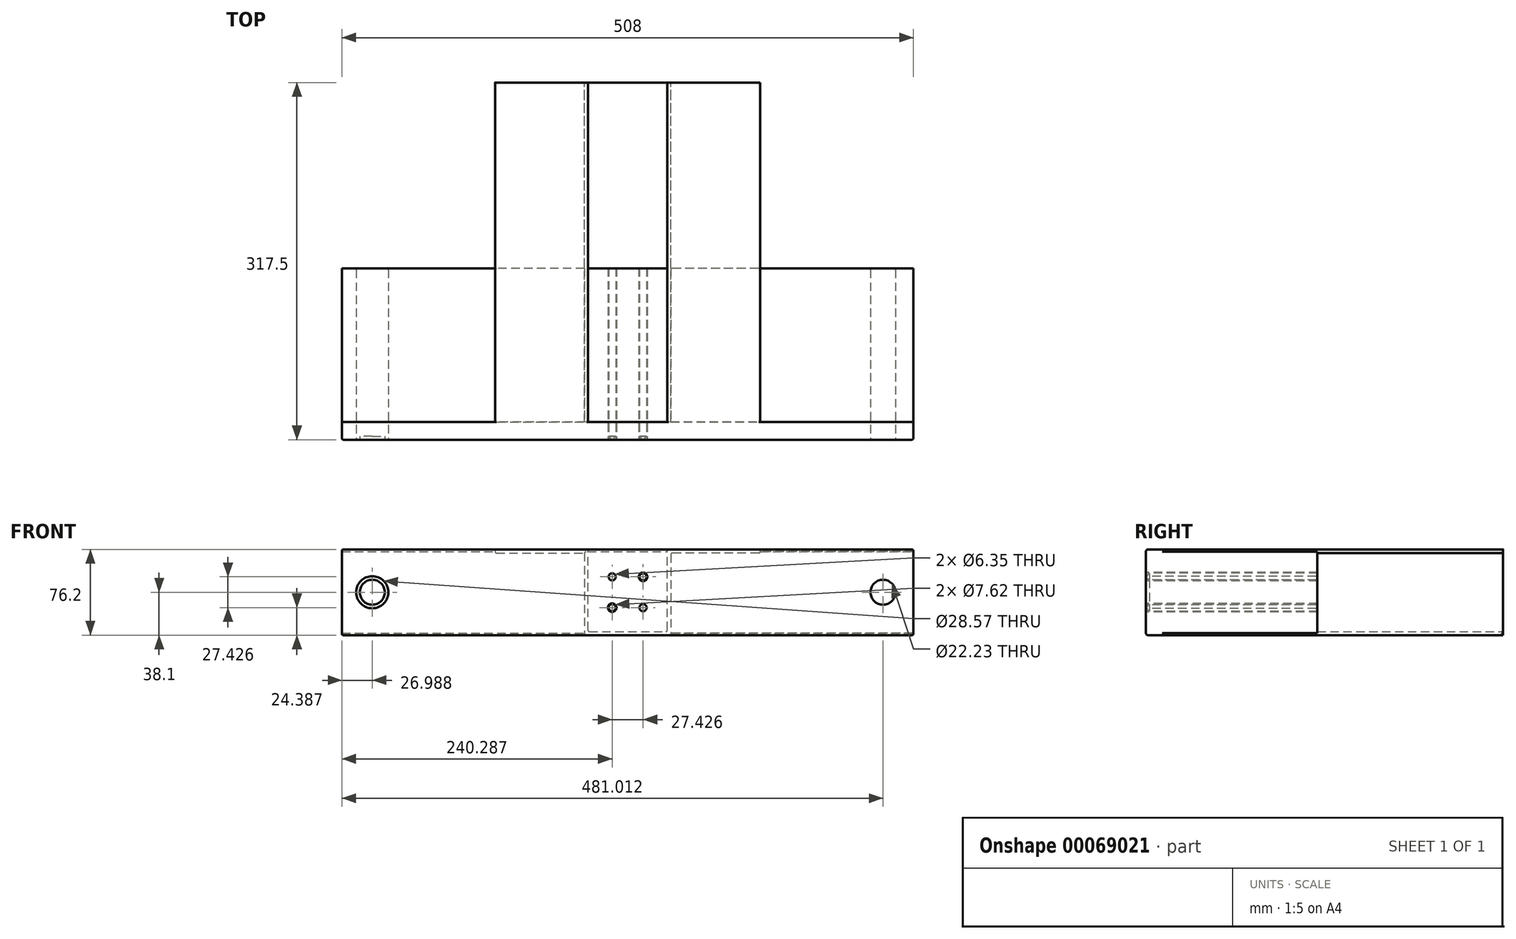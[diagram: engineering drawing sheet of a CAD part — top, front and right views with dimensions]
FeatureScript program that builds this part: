
annotation { "Feature Type Name" : "Feature", "Feature Type Description" : "" }
export const myFeature = defineFeature(function(context is Context, id is Id, definition is map)
    precondition{}
    {
        {
            var Q0;
            Q0=qCreatedBy(makeId("Front.planeOp"),FACE);
            var sketch = newSketch(context, id + "F0", { "sketchPlane" : qUnion([Q0])});
            skLineSegment(sketch, "E0.bottom", {"start": v(-508, 76.2) * mm, "end": v(0, 76.2) * mm});
            skLineSegment(sketch, "E0.top", {"start": v(-508, 0) * mm, "end": v(0, 0) * mm});
            skLineSegment(sketch, "E0.left", {"start": v(-508, 76.2) * mm, "end": v(-508, 0) * mm});
            skLineSegment(sketch, "E0.right", {"start": v(0, 76.2) * mm, "end": v(0, 0) * mm});
            skSolve(sketch);
        }
        {
            var Q0;
            Q0=makeQuery(id+"F0.imprint","IMPRINT",FACE,{"disambiguationData":[TD([[makeQuery(id+"F0.imprint","IMPRINT",EDGE,{"derivedFrom":sQuery(id+"F0.wireOp",EDGE,"E0.bottom")}),-1.0]])]});
            extrude(context, id + "F1", {"entities" : qUnion([Q0]), "depth" : 317.5 * mm});
        }
        {
            var Q0;
            Q0=makeQuery(id+"F1.opExtrude","SWEPT_FACE",FACE,{"disambiguationData":[OSD([sQuery(id+"F0.wireOp",EDGE,"E0.left")])]});
            var sketch = newSketch(context, id + "F2", { "sketchPlane" : qUnion([Q0])});
            skCircle(sketch, "E1", {"center": v(315.64, 74.34) * mm, "radius": 1.86 * mm});
            skCircle(sketch, "E2", {"center": v(312.47, 71.17) * mm, "radius": 1.86 * mm});
            skLineSegment(sketch, "E3.0", {"start": v(317.5, 76.2) * mm, "end": v(317.5, 0) * mm});
            skLineSegment(sketch, "E3.1", {"start": v(317.5, 76.2) * mm, "end": v(0, 76.2) * mm});
            skLineSegment(sketch, "E3.2", {"start": v(317.5, 0) * mm, "end": v(0, 0) * mm});
            skLineSegment(sketch, "E4", {"start": v(301.63, 76.2) * mm, "end": v(301.63, 73.03) * mm});
            skLineSegment(sketch, "E5", {"start": v(301.63, 73.03) * mm, "end": v(314.33, 73.03) * mm});
            skLineSegment(sketch, "E6", {"start": v(314.33, 73.03) * mm, "end": v(314.33, 3.18) * mm});
            skLineSegment(sketch, "E7", {"start": v(314.33, 3.18) * mm, "end": v(301.63, 3.18) * mm});
            skLineSegment(sketch, "E8", {"start": v(301.63, 3.18) * mm, "end": v(301.63, 0) * mm});
            skLineSegment(sketch, "E9", {"start": v(317.5, 38.1) * mm, "end": v(282.6, 38.1) * mm, "construction": true});
            skPoint(sketch, "E9.endSnap0", {"position": v(317.5, 38.1) * mm});
            skCircle(sketch, "E10.MirrorC", {"center": v(312.47, 5.03) * mm, "radius": 1.86 * mm});
            skCircle(sketch, "E11.MirrorC", {"center": v(315.64, 1.86) * mm, "radius": 1.86 * mm});
            skSolve(sketch);
        }
        {
            var Q0;
            Q0=makeQuery(id+"F1.opExtrude","CAP_FACE",FACE,{"disambiguationData":[OSD([sQuery(id+"F0.wireOp",EDGE,"E0.bottom"),sQuery(id+"F0.wireOp",EDGE,"E0.top"),sQuery(id+"F0.wireOp",EDGE,"E0.left"),sQuery(id+"F0.wireOp",EDGE,"E0.right")])],"isStart":true});
            var sketch = newSketch(context, id + "F3", { "sketchPlane" : qUnion([Q0])});
            skLineSegment(sketch, "E12.0", {"start": v(508, 76.2) * mm, "end": v(0, 76.2) * mm});
            skLineSegment(sketch, "E12.1", {"start": v(0, 76.2) * mm, "end": v(0, 0) * mm});
            skLineSegment(sketch, "E12.2", {"start": v(508, 0) * mm, "end": v(0, 0) * mm});
            skLineSegment(sketch, "E12.3", {"start": v(508, 76.2) * mm, "end": v(508, 0) * mm});
            skLineSegment(sketch, "E13", {"start": v(136.13, 76.2) * mm, "end": v(136.13, 73.03) * mm});
            skLineSegment(sketch, "E14", {"start": v(136.13, 73.03) * mm, "end": v(215.5, 73.03) * mm});
            skLineSegment(sketch, "E15", {"start": v(215.5, 73.03) * mm, "end": v(215.5, 0) * mm});
            skLineSegment(sketch, "E16", {"start": v(215.5, 0) * mm, "end": v(254, 0) * mm});
            skLineSegment(sketch, "E17", {"start": v(254, 0) * mm, "end": v(254, 3.17) * mm});
            skLineSegment(sketch, "E18", {"start": v(254, 3.17) * mm, "end": v(218.68, 3.17) * mm});
            skLineSegment(sketch, "E19", {"start": v(218.68, 3.17) * mm, "end": v(218.68, 76.2) * mm});
            skLineSegment(sketch, "E20", {"start": v(218.68, 76.2) * mm, "end": v(136.13, 76.2) * mm});
            skLineSegment(sketch, "E21", {"start": v(254, 76.2) * mm, "end": v(254, 0) * mm, "construction": true});
            skLineSegment(sketch, "E22.MirrorCS", {"start": v(292.5, 0) * mm, "end": v(254, 0) * mm});
            skLineSegment(sketch, "E23.MirrorCS", {"start": v(254, 3.17) * mm, "end": v(289.32, 3.17) * mm});
            skLineSegment(sketch, "E24.MirrorCS", {"start": v(289.32, 3.17) * mm, "end": v(289.32, 76.2) * mm});
            skLineSegment(sketch, "E25.MirrorCS", {"start": v(292.5, 73.03) * mm, "end": v(292.5, 0) * mm});
            skLineSegment(sketch, "E26.MirrorCS", {"start": v(289.32, 76.2) * mm, "end": v(371.87, 76.2) * mm});
            skLineSegment(sketch, "E27.MirrorCS", {"start": v(371.87, 73.03) * mm, "end": v(292.5, 73.03) * mm});
            skLineSegment(sketch, "E28.MirrorCS", {"start": v(371.87, 76.2) * mm, "end": v(371.87, 73.03) * mm});
            skSolve(sketch);
        }
        {
            var Q0;
            {var subQ2=sQuery(id+"F2.wireOp",EDGE,"E4");Q0=makeQuery(id+"F2.imprint","IMPRINT",FACE,{"disambiguationData":[TD([[makeQuery(id+"F2.imprint","IMPRINT",EDGE,{"derivedFrom":subQ2}),-1.0]])]});}
            var Q1;
            {var subQ0=sQuery(id+"F2.wireOp",EDGE,"E3.1");var subQ1=sQuery(id+"F2.wireOp",EDGE,"E1");var subQ2=makeQuery(id+"F2.imprint","INTERSECT",VERTEX,{"derivedFrom":[subQ1,subQ0]});Q1=makeQuery(id+"F2.imprint","IMPRINT",FACE,{"disambiguationData":[TD([[makeQuery(id+"F2.imprint","IMPRINT",EDGE,{"disambiguationData":[TD([[subQ2,1.0]])],"derivedFrom":subQ1}),-1.0]])]});}
            var Q2;
            {var subQ0=sQuery(id+"F2.wireOp",EDGE,"E2");var subQ1=makeQuery(id+"F2.imprint","INTERSECT",VERTEX,{"derivedFrom":[subQ0,sQuery(id+"F2.wireOp",EDGE,"E5")]});Q2=makeQuery(id+"F2.imprint","IMPRINT",FACE,{"disambiguationData":[TD([[makeQuery(id+"F2.imprint","IMPRINT",EDGE,{"disambiguationData":[TD([[subQ1,1.0]])],"derivedFrom":subQ0}),1.0]])]});}
            var Q3;
            {var subQ0=sQuery(id+"F2.wireOp",EDGE,"E3.2");var subQ1=sQuery(id+"F2.wireOp",EDGE,"E3.0");var subQ2=makeQuery(id+"F2.imprint","INTERSECT",VERTEX,{"derivedFrom":[subQ1,subQ0]});Q3=makeQuery(id+"F2.imprint","IMPRINT",FACE,{"disambiguationData":[TD([[makeQuery(id+"F2.imprint","IMPRINT",EDGE,{"disambiguationData":[TD([[subQ2,1.0]])],"derivedFrom":subQ1}),-1.0]])]});}
            var Q4;
            {var subQ0=sQuery(id+"F2.wireOp",EDGE,"E10.MirrorC");var subQ1=makeQuery(id+"F2.imprint","INTERSECT",VERTEX,{"derivedFrom":[sQuery(id+"F2.wireOp",EDGE,"E6"),subQ0]});Q4=makeQuery(id+"F2.imprint","IMPRINT",FACE,{"disambiguationData":[TD([[makeQuery(id+"F2.imprint","IMPRINT",EDGE,{"disambiguationData":[TD([[subQ1,-1.0]])],"derivedFrom":subQ0}),-1.0]])]});}
            extrude(context, id + "F4", {"entities" : qUnion([Q0, Q1, Q2, Q3, Q4]), "operationType" : NewBodyOperationType.REMOVE, "endBound" : BoundingType.THROUGH_ALL, "oppositeDirection" : true, "depth" : 25.4 * mm});
        }
        {
            var Q0;
            Q0=makeQuery(id+"F3.imprint","IMPRINT",FACE,{"disambiguationData":[TD([[makeQuery(id+"F3.imprint","IMPRINT",EDGE,{"derivedFrom":sQuery(id+"F3.wireOp",EDGE,"E13")}),1.0]])]});
            var Q1;
            Q1=makeQuery(id+"F3.imprint","IMPRINT",FACE,{"disambiguationData":[TD([[makeQuery(id+"F3.imprint","IMPRINT",EDGE,{"derivedFrom":sQuery(id+"F3.wireOp",EDGE,"E17")}),-1.0]])]});
            var Q2;
            Q2=makeQuery(id+"F4.boolean.opBoolean","COPY",FACE,{"derivedFrom":makeQuery(id+"F4.opExtrude","SWEPT_FACE",FACE,{"disambiguationData":[OSD([sQuery(id+"F2.wireOp",EDGE,"E6")])]})});
            extrude(context, id + "F5", {"entities" : qUnion([Q0, Q1]), "operationType" : NewBodyOperationType.ADD, "endBound" : BoundingType.UP_TO_SURFACE, "oppositeDirection" : true, "endBoundEntityFace" : qUnion([Q2]), "depth" : 25.4 * mm});
        }
        {
            var Q0;
            Q0=makeQuery(id+"F1.opExtrude","CAP_FACE",FACE,{"disambiguationData":[OSD([sQuery(id+"F0.wireOp",EDGE,"E0.bottom"),sQuery(id+"F0.wireOp",EDGE,"E0.top"),sQuery(id+"F0.wireOp",EDGE,"E0.left"),sQuery(id+"F0.wireOp",EDGE,"E0.right")])],"isStart":false});
            var sketch = newSketch(context, id + "F6", { "sketchPlane" : qUnion([Q0])});
            skLineSegment(sketch, "E29.0", {"start": v(0, 0) * mm, "end": v(-508, 0) * mm});
            skLineSegment(sketch, "E29.1", {"start": v(0, 74.34) * mm, "end": v(-508, 74.34) * mm});
            skLineSegment(sketch, "E30", {"start": v(0, 1.86) * mm, "end": v(-508, 74.34) * mm, "construction": true});
            skCircle(sketch, "E31", {"center": v(-254, 38.1) * mm, "radius": 19.4 * mm, "construction": true});
            skCircle(sketch, "E32", {"center": v(-240.29, 24.39) * mm, "radius": 3.81 * mm});
            skCircle(sketch, "E33", {"center": v(-240.29, 24.39) * mm, "radius": 3.18 * mm});
            skLineSegment(sketch, "E34", {"start": v(-254, 1.86) * mm, "end": v(-254, 74.34) * mm, "construction": true});
            skLineSegment(sketch, "E35", {"start": v(-303.81, 38.1) * mm, "end": v(-196.21, 38.1) * mm, "construction": true});
            skLineSegment(sketch, "E36", {"start": v(-254, 38.1) * mm, "end": v(-240.29, 24.39) * mm, "construction": true});
            skCircle(sketch, "E37.MirrorC", {"center": v(-267.71, 24.39) * mm, "radius": 3.81 * mm});
            skCircle(sketch, "E38.MirrorC", {"center": v(-267.71, 24.39) * mm, "radius": 3.18 * mm});
            skCircle(sketch, "E39.MirrorC", {"center": v(-267.71, 51.81) * mm, "radius": 3.81 * mm});
            skCircle(sketch, "E40.MirrorC", {"center": v(-267.71, 51.81) * mm, "radius": 3.18 * mm});
            skCircle(sketch, "E41.MirrorC", {"center": v(-240.29, 51.81) * mm, "radius": 3.81 * mm});
            skCircle(sketch, "E42.MirrorC", {"center": v(-240.29, 51.81) * mm, "radius": 3.18 * mm});
            skSolve(sketch);
        }
        {
            var Q0;
            Q0=makeQuery(id+"F6.imprint","IMPRINT",FACE,{"disambiguationData":[TD([[makeQuery(id+"F6.imprint","IMPRINT",EDGE,{"derivedFrom":sQuery(id+"F6.wireOp",EDGE,"E33")}),1.0]])]});
            var Q1;
            Q1=makeQuery(id+"F6.imprint","IMPRINT",FACE,{"disambiguationData":[TD([[makeQuery(id+"F6.imprint","IMPRINT",EDGE,{"derivedFrom":sQuery(id+"F6.wireOp",EDGE,"E38.MirrorC")}),-1.0]])]});
            var Q2;
            Q2=makeQuery(id+"F6.imprint","IMPRINT",FACE,{"disambiguationData":[TD([[makeQuery(id+"F6.imprint","IMPRINT",EDGE,{"derivedFrom":sQuery(id+"F6.wireOp",EDGE,"E40.MirrorC")}),1.0]])]});
            var Q3;
            Q3=makeQuery(id+"F6.imprint","IMPRINT",FACE,{"disambiguationData":[TD([[makeQuery(id+"F6.imprint","IMPRINT",EDGE,{"derivedFrom":sQuery(id+"F6.wireOp",EDGE,"E42.MirrorC")}),-1.0]])]});
            extrude(context, id + "F7", {"entities" : qUnion([Q0, Q1, Q2, Q3]), "operationType" : NewBodyOperationType.REMOVE, "endBound" : BoundingType.THROUGH_ALL, "oppositeDirection" : true, "depth" : 25.4 * mm});
        }
        {
            var Q0;
            Q0=makeQuery(id+"F7.boolean.opBoolean","COPY",EDGE,{"derivedFrom":makeQuery(id+"F7.opExtrude","CAP_EDGE",EDGE,{"disambiguationData":[OSD([sQuery(id+"F6.wireOp",EDGE,"E33")])],"isStart":true})});
            var Q1;
            Q1=makeQuery(id+"F7.boolean.opBoolean","COPY",EDGE,{"derivedFrom":makeQuery(id+"F7.opExtrude","CAP_EDGE",EDGE,{"disambiguationData":[OSD([sQuery(id+"F6.wireOp",EDGE,"E38.MirrorC")])],"isStart":true})});
            var Q2;
            Q2=makeQuery(id+"F7.boolean.opBoolean","COPY",EDGE,{"derivedFrom":makeQuery(id+"F7.opExtrude","CAP_EDGE",EDGE,{"disambiguationData":[OSD([sQuery(id+"F6.wireOp",EDGE,"E40.MirrorC")])],"isStart":true})});
            var Q3;
            Q3=makeQuery(id+"F7.boolean.opBoolean","COPY",EDGE,{"derivedFrom":makeQuery(id+"F7.opExtrude","CAP_EDGE",EDGE,{"disambiguationData":[OSD([sQuery(id+"F6.wireOp",EDGE,"E42.MirrorC")])],"isStart":true})});
            chamfer(context, id + "F8", {"entities" : qUnion([Q0, Q1, Q2, Q3]), "width" : 3.17 * mm, "tangentPropagation" : true});
        }
        {
            var Q0;
            Q0=makeQuery(id+"F1.opExtrude","CAP_FACE",FACE,{"disambiguationData":[OSD([sQuery(id+"F0.wireOp",EDGE,"E0.bottom"),sQuery(id+"F0.wireOp",EDGE,"E0.top"),sQuery(id+"F0.wireOp",EDGE,"E0.left"),sQuery(id+"F0.wireOp",EDGE,"E0.right")])],"isStart":false});
            var sketch = newSketch(context, id + "F9", { "sketchPlane" : qUnion([Q0])});
            skLineSegment(sketch, "E43.0", {"start": v(0, 1.86) * mm, "end": v(-508, 1.86) * mm});
            skLineSegment(sketch, "E43.1", {"start": v(0, 74.34) * mm, "end": v(-508, 74.34) * mm});
            skLineSegment(sketch, "E44", {"start": v(-254, 1.86) * mm, "end": v(-254, 74.34) * mm, "construction": true});
            skLineSegment(sketch, "E45.0", {"start": v(0, 74.34) * mm, "end": v(0, 1.86) * mm});
            skLineSegment(sketch, "E45.1", {"start": v(-508, 74.34) * mm, "end": v(-508, 1.86) * mm});
            skLineSegment(sketch, "E46", {"start": v(0, 38.1) * mm, "end": v(-254, 38.1) * mm, "construction": true});
            skCircle(sketch, "E47", {"center": v(-26.99, 38.1) * mm, "radius": 11.11 * mm});
            skCircle(sketch, "E48.MirrorC", {"center": v(-481.01, 38.1) * mm, "radius": 11.11 * mm});
            skCircle(sketch, "E49", {"center": v(-26.99, 38.1) * mm, "radius": 14.29 * mm});
            skCircle(sketch, "E50.MirrorC", {"center": v(-481.01, 38.1) * mm, "radius": 14.29 * mm});
            skSolve(sketch);
        }
        {
            var Q0;
            Q0=makeQuery(id+"F9.imprint","IMPRINT",FACE,{"disambiguationData":[TD([[makeQuery(id+"F9.imprint","IMPRINT",EDGE,{"derivedFrom":sQuery(id+"F9.wireOp",EDGE,"E47")}),-1.0]])]});
            var Q1;
            Q1=makeQuery(id+"F9.imprint","IMPRINT",FACE,{"disambiguationData":[TD([[makeQuery(id+"F9.imprint","IMPRINT",EDGE,{"derivedFrom":sQuery(id+"F9.wireOp",EDGE,"E50.MirrorC")}),-1.0]])]});
            extrude(context, id + "F10", {"entities" : qUnion([Q0, Q1]), "operationType" : NewBodyOperationType.ADD, "oppositeDirection" : true, "depth" : 152.4 * mm});
        }
        {
            var Q0;
            Q0=makeQuery(id+"F9.imprint","IMPRINT",FACE,{"disambiguationData":[TD([[makeQuery(id+"F9.imprint","IMPRINT",EDGE,{"derivedFrom":sQuery(id+"F9.wireOp",EDGE,"E47")}),1.0]])]});
            var Q1;
            Q1=makeQuery(id+"F9.imprint","IMPRINT",FACE,{"disambiguationData":[TD([[makeQuery(id+"F9.imprint","IMPRINT",EDGE,{"derivedFrom":sQuery(id+"F9.wireOp",EDGE,"E48.MirrorC")}),-1.0]])]});
            extrude(context, id + "F11", {"entities" : qUnion([Q0, Q1]), "operationType" : NewBodyOperationType.REMOVE, "endBound" : BoundingType.THROUGH_ALL, "oppositeDirection" : true, "depth" : 25.4 * mm});
        }
        {
            var Q0;
            Q0=makeQuery(id+"F4.boolean.opBoolean","COPY",EDGE,{"derivedFrom":makeQuery(id+"F4.opExtrude","CAP_EDGE",EDGE,{"disambiguationData":[OSD([sQuery(id+"F2.wireOp",EDGE,"E8")])],"isStart":true})});
            var Q1;
            Q1=makeQuery(id+"F4.boolean.opBoolean","COPY",EDGE,{"derivedFrom":makeQuery(id+"F4.opExtrude","CAP_EDGE",EDGE,{"disambiguationData":[OSD([sQuery(id+"F2.wireOp",EDGE,"E4")])],"isStart":true})});
            var Q2;
            Q2=makeQuery(id+"F4.boolean.opBoolean","INTERSECT",EDGE,{"derivedFrom":[makeQuery(id+"F1.opExtrude","SWEPT_FACE",FACE,{"disambiguationData":[OSD([sQuery(id+"F0.wireOp",EDGE,"E0.right")])]}),makeQuery(id+"F4.opExtrude","SWEPT_FACE",FACE,{"disambiguationData":[OSD([sQuery(id+"F2.wireOp",EDGE,"E8")])]})]});
            var Q3;
            Q3=makeQuery(id+"F4.boolean.opBoolean","INTERSECT",EDGE,{"derivedFrom":[makeQuery(id+"F1.opExtrude","SWEPT_FACE",FACE,{"disambiguationData":[OSD([sQuery(id+"F0.wireOp",EDGE,"E0.right")])]}),makeQuery(id+"F4.opExtrude","SWEPT_FACE",FACE,{"disambiguationData":[OSD([sQuery(id+"F2.wireOp",EDGE,"E4")])]})]});
            var Q4;
            Q4=makeQuery(id+"F10.opExtrude","CAP_EDGE",EDGE,{"disambiguationData":[OSD([sQuery(id+"F9.wireOp",EDGE,"E47")])],"isStart":false});
            var Q5;
            Q5=makeQuery(id+"F11.boolean.opBoolean","COPY",EDGE,{"derivedFrom":makeQuery(id+"F11.opExtrude","CAP_EDGE",EDGE,{"disambiguationData":[OSD([sQuery(id+"F9.wireOp",EDGE,"E47")])],"isStart":true})});
            var Q6;
            Q6=makeQuery(id+"F11.boolean.opBoolean","COPY",EDGE,{"derivedFrom":makeQuery(id+"F11.opExtrude","CAP_EDGE",EDGE,{"disambiguationData":[OSD([sQuery(id+"F9.wireOp",EDGE,"E48.MirrorC")])],"isStart":true})});
            var Q7;
            Q7=makeQuery(id+"F10.opExtrude","CAP_EDGE",EDGE,{"disambiguationData":[OSD([sQuery(id+"F9.wireOp",EDGE,"E48.MirrorC")])],"isStart":false});
            var Q8;
            Q8=makeQuery(id+"F10.opExtrude","CAP_EDGE",EDGE,{"disambiguationData":[OSD([sQuery(id+"F9.wireOp",EDGE,"E50.MirrorC")])],"isStart":false});
            var Q9;
            Q9=makeQuery(id+"F10.opExtrude","CAP_EDGE",EDGE,{"disambiguationData":[OSD([sQuery(id+"F9.wireOp",EDGE,"E49")])],"isStart":false});
            var Q10;
            {var subQ0=sQuery(id+"F2.wireOp",EDGE,"E8");Q10=makeQuery(id+"F5.boolean.opBoolean","SPLIT",EDGE,{"disambiguationData":[TD([makeQuery(id+"F1.opExtrude","SWEPT_FACE",FACE,{"disambiguationData":[OSD([sQuery(id+"F0.wireOp",EDGE,"E0.right")])]})])],"derivedFrom":makeQuery(id+"F4.boolean.opBoolean","COPY",EDGE,{"derivedFrom":makeQuery(id+"F4.opExtrude","SWEPT_EDGE",EDGE,{"disambiguationData":[OSD([sQuery(id+"F2.wireOp",EDGE,"E3.2"),subQ0])]})})});}
            var Q11;
            {var subQ0=sQuery(id+"F2.wireOp",EDGE,"E8");var subQ1=sQuery(id+"F2.wireOp",EDGE,"E7");Q11=makeQuery(id+"F5.boolean.opBoolean","SPLIT",EDGE,{"disambiguationData":[TD([makeQuery(id+"F1.opExtrude","SWEPT_FACE",FACE,{"disambiguationData":[OSD([sQuery(id+"F0.wireOp",EDGE,"E0.right")])]})])],"derivedFrom":makeQuery(id+"F4.boolean.opBoolean","COPY",EDGE,{"derivedFrom":makeQuery(id+"F4.opExtrude","SWEPT_EDGE",EDGE,{"disambiguationData":[OSD([subQ1,subQ0])]})})});}
            var Q12;
            {var subQ0=sQuery(id+"F2.wireOp",EDGE,"E5");var subQ1=sQuery(id+"F2.wireOp",EDGE,"E4");Q12=makeQuery(id+"F5.boolean.opBoolean","SPLIT",EDGE,{"disambiguationData":[TD([makeQuery(id+"F1.opExtrude","SWEPT_FACE",FACE,{"disambiguationData":[OSD([sQuery(id+"F0.wireOp",EDGE,"E0.right")])]})])],"derivedFrom":makeQuery(id+"F4.boolean.opBoolean","COPY",EDGE,{"derivedFrom":makeQuery(id+"F4.opExtrude","SWEPT_EDGE",EDGE,{"disambiguationData":[OSD([subQ1,subQ0])]})})});}
            var Q13;
            {var subQ0=sQuery(id+"F2.wireOp",EDGE,"E4");Q13=makeQuery(id+"F5.boolean.opBoolean","SPLIT",EDGE,{"disambiguationData":[TD([makeQuery(id+"F1.opExtrude","SWEPT_FACE",FACE,{"disambiguationData":[OSD([sQuery(id+"F0.wireOp",EDGE,"E0.right")])]})])],"derivedFrom":makeQuery(id+"F4.boolean.opBoolean","COPY",EDGE,{"derivedFrom":makeQuery(id+"F4.opExtrude","SWEPT_EDGE",EDGE,{"disambiguationData":[OSD([sQuery(id+"F2.wireOp",EDGE,"E3.1"),subQ0])]})})});}
            var Q14;
            {var subQ0=sQuery(id+"F2.wireOp",EDGE,"E5");var subQ1=sQuery(id+"F2.wireOp",EDGE,"E4");Q14=makeQuery(id+"F5.boolean.opBoolean","SPLIT",EDGE,{"disambiguationData":[TD([makeQuery(id+"F1.opExtrude","SWEPT_FACE",FACE,{"disambiguationData":[OSD([sQuery(id+"F0.wireOp",EDGE,"E0.left")])]})])],"derivedFrom":makeQuery(id+"F4.boolean.opBoolean","COPY",EDGE,{"derivedFrom":makeQuery(id+"F4.opExtrude","SWEPT_EDGE",EDGE,{"disambiguationData":[OSD([subQ1,subQ0])]})})});}
            var Q15;
            {var subQ0=sQuery(id+"F2.wireOp",EDGE,"E4");Q15=makeQuery(id+"F5.boolean.opBoolean","SPLIT",EDGE,{"disambiguationData":[TD([makeQuery(id+"F1.opExtrude","SWEPT_FACE",FACE,{"disambiguationData":[OSD([sQuery(id+"F0.wireOp",EDGE,"E0.left")])]})])],"derivedFrom":makeQuery(id+"F4.boolean.opBoolean","COPY",EDGE,{"derivedFrom":makeQuery(id+"F4.opExtrude","SWEPT_EDGE",EDGE,{"disambiguationData":[OSD([sQuery(id+"F2.wireOp",EDGE,"E3.1"),subQ0])]})})});}
            var Q16;
            Q16=makeQuery(id+"F5.opExtrude","SWEPT_EDGE",EDGE,{"disambiguationData":[OSD([sQuery(id+"F3.wireOp",EDGE,"E27.MirrorCS"),sQuery(id+"F3.wireOp",EDGE,"E28.MirrorCS")])]});
            var Q17;
            Q17=makeQuery(id+"F5.opExtrude","SWEPT_EDGE",EDGE,{"disambiguationData":[OSD([sQuery(id+"F3.wireOp",EDGE,"E12.0"),sQuery(id+"F3.wireOp",EDGE,"E26.MirrorCS"),sQuery(id+"F3.wireOp",EDGE,"E28.MirrorCS")])]});
            var Q18;
            Q18=makeQuery(id+"F5.opExtrude","CAP_EDGE",EDGE,{"disambiguationData":[OSD([sQuery(id+"F3.wireOp",EDGE,"E27.MirrorCS")])],"isStart":true});
            var Q19;
            Q19=makeQuery(id+"F5.opExtrude","CAP_EDGE",EDGE,{"disambiguationData":[OSD([sQuery(id+"F3.wireOp",EDGE,"E26.MirrorCS")])],"isStart":true});
            var Q20;
            Q20=makeQuery(id+"F5.opExtrude","CAP_EDGE",EDGE,{"disambiguationData":[OSD([sQuery(id+"F3.wireOp",EDGE,"E25.MirrorCS")])],"isStart":true});
            var Q21;
            Q21=makeQuery(id+"F5.opExtrude","CAP_EDGE",EDGE,{"disambiguationData":[OSD([sQuery(id+"F3.wireOp",EDGE,"E24.MirrorCS")])],"isStart":true});
            var Q22;
            Q22=makeQuery(id+"F5.opExtrude","CAP_EDGE",EDGE,{"disambiguationData":[OSD([sQuery(id+"F3.wireOp",EDGE,"E16"),sQuery(id+"F3.wireOp",EDGE,"E22.MirrorCS")])],"isStart":true});
            var Q23;
            Q23=makeQuery(id+"F5.opExtrude","CAP_EDGE",EDGE,{"disambiguationData":[OSD([sQuery(id+"F3.wireOp",EDGE,"E18"),sQuery(id+"F3.wireOp",EDGE,"E23.MirrorCS")])],"isStart":true});
            var Q24;
            Q24=makeQuery(id+"F5.opExtrude","CAP_EDGE",EDGE,{"disambiguationData":[OSD([sQuery(id+"F3.wireOp",EDGE,"E15")])],"isStart":true});
            var Q25;
            Q25=makeQuery(id+"F5.opExtrude","CAP_EDGE",EDGE,{"disambiguationData":[OSD([sQuery(id+"F3.wireOp",EDGE,"E20")])],"isStart":true});
            var Q26;
            Q26=makeQuery(id+"F5.opExtrude","CAP_EDGE",EDGE,{"disambiguationData":[OSD([sQuery(id+"F3.wireOp",EDGE,"E19")])],"isStart":true});
            var Q27;
            Q27=makeQuery(id+"F5.opExtrude","CAP_EDGE",EDGE,{"disambiguationData":[OSD([sQuery(id+"F3.wireOp",EDGE,"E14")])],"isStart":true});
            var Q28;
            Q28=makeQuery(id+"F5.opExtrude","SWEPT_EDGE",EDGE,{"disambiguationData":[OSD([sQuery(id+"F3.wireOp",EDGE,"E13"),sQuery(id+"F3.wireOp",EDGE,"E14")])]});
            var Q29;
            Q29=makeQuery(id+"F5.opExtrude","SWEPT_EDGE",EDGE,{"disambiguationData":[OSD([sQuery(id+"F3.wireOp",EDGE,"E12.0"),sQuery(id+"F3.wireOp",EDGE,"E13"),sQuery(id+"F3.wireOp",EDGE,"E20")])]});
            var Q30;
            Q30=makeQuery(id+"F5.opExtrude","SWEPT_EDGE",EDGE,{"disambiguationData":[OSD([sQuery(id+"F3.wireOp",EDGE,"E12.2"),sQuery(id+"F3.wireOp",EDGE,"E15"),sQuery(id+"F3.wireOp",EDGE,"E16")])]});
            var Q31;
            Q31=makeQuery(id+"F5.opExtrude","SWEPT_EDGE",EDGE,{"disambiguationData":[OSD([sQuery(id+"F3.wireOp",EDGE,"E12.2"),sQuery(id+"F3.wireOp",EDGE,"E22.MirrorCS"),sQuery(id+"F3.wireOp",EDGE,"E25.MirrorCS")])]});
            var Q32;
            {var subQ0=sQuery(id+"F2.wireOp",EDGE,"E8");Q32=makeQuery(id+"F5.boolean.opBoolean","SPLIT",EDGE,{"disambiguationData":[TD([makeQuery(id+"F1.opExtrude","SWEPT_FACE",FACE,{"disambiguationData":[OSD([sQuery(id+"F0.wireOp",EDGE,"E0.left")])]})])],"derivedFrom":makeQuery(id+"F4.boolean.opBoolean","COPY",EDGE,{"derivedFrom":makeQuery(id+"F4.opExtrude","SWEPT_EDGE",EDGE,{"disambiguationData":[OSD([sQuery(id+"F2.wireOp",EDGE,"E3.2"),subQ0])]})})});}
            var Q33;
            {var subQ0=sQuery(id+"F2.wireOp",EDGE,"E8");var subQ1=sQuery(id+"F2.wireOp",EDGE,"E7");Q33=makeQuery(id+"F5.boolean.opBoolean","SPLIT",EDGE,{"disambiguationData":[TD([makeQuery(id+"F1.opExtrude","SWEPT_FACE",FACE,{"disambiguationData":[OSD([sQuery(id+"F0.wireOp",EDGE,"E0.left")])]})])],"derivedFrom":makeQuery(id+"F4.boolean.opBoolean","COPY",EDGE,{"derivedFrom":makeQuery(id+"F4.opExtrude","SWEPT_EDGE",EDGE,{"disambiguationData":[OSD([subQ1,subQ0])]})})});}
            var Q34;
            Q34=makeQuery(id+"F5.opExtrude","SWEPT_EDGE",EDGE,{"disambiguationData":[OSD([sQuery(id+"F3.wireOp",EDGE,"E14"),sQuery(id+"F3.wireOp",EDGE,"E15")])]});
            var Q35;
            Q35=makeQuery(id+"F5.opExtrude","SWEPT_EDGE",EDGE,{"disambiguationData":[OSD([sQuery(id+"F3.wireOp",EDGE,"E25.MirrorCS"),sQuery(id+"F3.wireOp",EDGE,"E27.MirrorCS")])]});
            var Q36;
            Q36=makeQuery(id+"F5.opExtrude","SWEPT_EDGE",EDGE,{"disambiguationData":[OSD([sQuery(id+"F3.wireOp",EDGE,"E12.0"),sQuery(id+"F3.wireOp",EDGE,"E19"),sQuery(id+"F3.wireOp",EDGE,"E20")])]});
            var Q37;
            Q37=makeQuery(id+"F5.opExtrude","SWEPT_EDGE",EDGE,{"disambiguationData":[OSD([sQuery(id+"F3.wireOp",EDGE,"E18"),sQuery(id+"F3.wireOp",EDGE,"E19")])]});
            var Q38;
            Q38=makeQuery(id+"F5.opExtrude","SWEPT_EDGE",EDGE,{"disambiguationData":[OSD([sQuery(id+"F3.wireOp",EDGE,"E23.MirrorCS"),sQuery(id+"F3.wireOp",EDGE,"E24.MirrorCS")])]});
            var Q39;
            Q39=makeQuery(id+"F5.opExtrude","SWEPT_EDGE",EDGE,{"disambiguationData":[OSD([sQuery(id+"F3.wireOp",EDGE,"E12.0"),sQuery(id+"F3.wireOp",EDGE,"E24.MirrorCS"),sQuery(id+"F3.wireOp",EDGE,"E26.MirrorCS")])]});
            var Q40;
            {var subQ0=sQuery(id+"F2.wireOp",EDGE,"E4");Q40=makeQuery(id+"F5.boolean.opBoolean","SPLIT",EDGE,{"disambiguationData":[TD([makeQuery(id+"F5.opExtrude","SWEPT_FACE",FACE,{"disambiguationData":[OSD([sQuery(id+"F3.wireOp",EDGE,"E19")])]})])],"derivedFrom":makeQuery(id+"F4.boolean.opBoolean","COPY",EDGE,{"derivedFrom":makeQuery(id+"F4.opExtrude","SWEPT_EDGE",EDGE,{"disambiguationData":[OSD([sQuery(id+"F2.wireOp",EDGE,"E3.1"),subQ0])]})})});}
            var Q41;
            {var subQ0=sQuery(id+"F2.wireOp",EDGE,"E4");var subQ1=sQuery(id+"F2.wireOp",EDGE,"E5");Q41=makeQuery(id+"F5.boolean.opBoolean","SPLIT",EDGE,{"disambiguationData":[TD([makeQuery(id+"F5.opExtrude","SWEPT_FACE",FACE,{"disambiguationData":[OSD([sQuery(id+"F3.wireOp",EDGE,"E19")])]})])],"derivedFrom":makeQuery(id+"F4.boolean.opBoolean","COPY",EDGE,{"derivedFrom":makeQuery(id+"F4.opExtrude","SWEPT_EDGE",EDGE,{"disambiguationData":[OSD([subQ0,subQ1])]})})});}
            var Q42;
            Q42=makeQuery(id+"F4.boolean.opBoolean","INTERSECT",EDGE,{"derivedFrom":[makeQuery(id+"F1.opExtrude","SWEPT_FACE",FACE,{"disambiguationData":[OSD([sQuery(id+"F0.wireOp",EDGE,"E0.right")])]}),makeQuery(id+"F4.opExtrude","SWEPT_FACE",FACE,{"disambiguationData":[OSD([sQuery(id+"F2.wireOp",EDGE,"E6")])]})]});
            var Q43;
            Q43=makeQuery(id+"F1.opExtrude","CAP_EDGE",EDGE,{"disambiguationData":[OSD([sQuery(id+"F0.wireOp",EDGE,"E0.right")])],"isStart":false});
            var Q44;
            Q44=makeQuery(id+"F4.boolean.opBoolean","COPY",EDGE,{"derivedFrom":makeQuery(id+"F4.opExtrude","CAP_EDGE",EDGE,{"disambiguationData":[OSD([sQuery(id+"F2.wireOp",EDGE,"E6")])],"isStart":true})});
            var Q45;
            Q45=makeQuery(id+"F1.opExtrude","SWEPT_EDGE",EDGE,{"disambiguationData":[OSD([sQuery(id+"F0.wireOp",EDGE,"E0.bottom"),sQuery(id+"F0.wireOp",EDGE,"E0.left")])]});
            fillet(context, id + "F12", {"entities" : qUnion([Q0, Q1, Q2, Q3, Q4, Q5, Q6, Q7, Q8, Q9, Q10, Q11, Q12, Q13, Q14, Q15, Q16, Q17, Q18, Q19, Q20, Q21, Q22, Q23, Q24, Q25, Q26, Q27, Q28, Q29, Q30, Q31, Q32, Q33, Q34, Q35, Q36, Q37, Q38, Q39, Q40, Q41, Q42, Q43, Q44, Q45]), "radius" : 1.27 * mm, "tangentPropagation" : true, "allowEdgeOverflow" : false});
        }
    });
